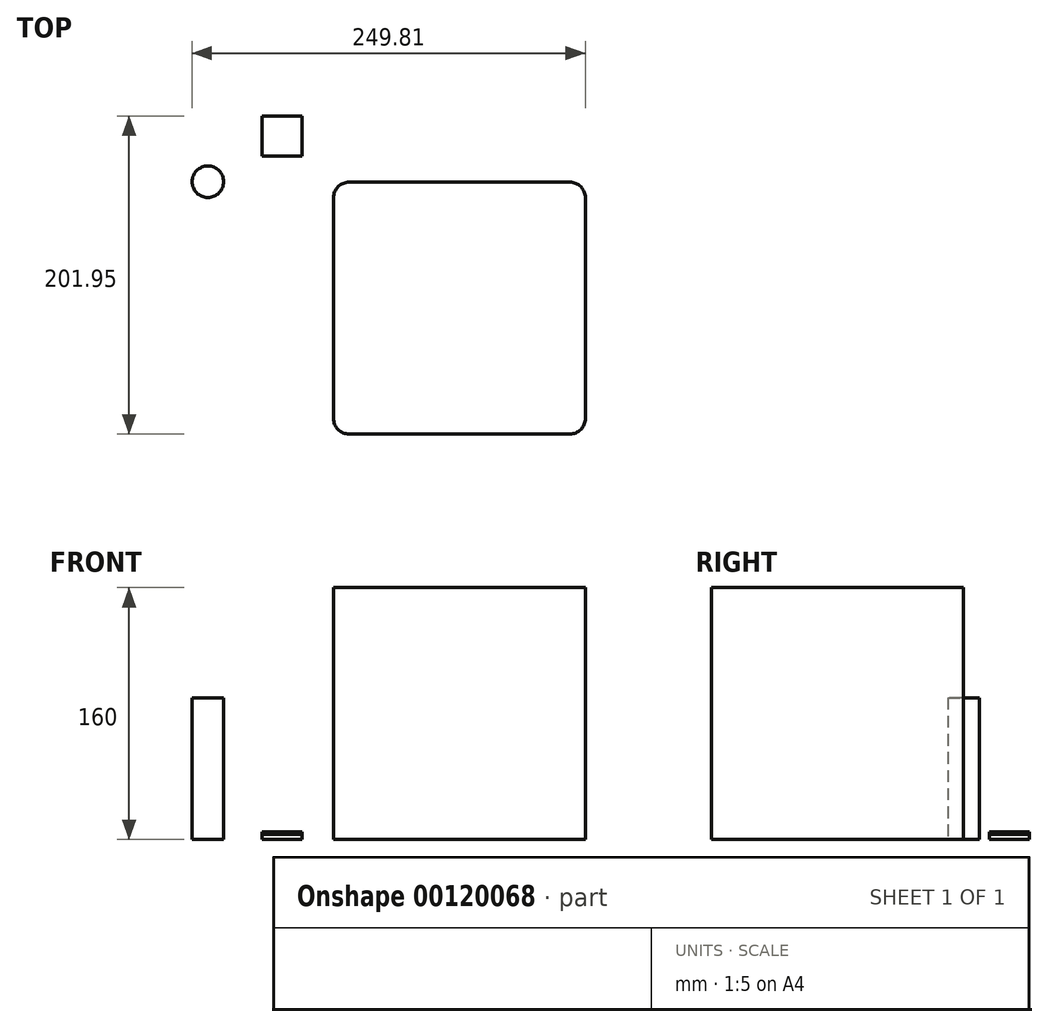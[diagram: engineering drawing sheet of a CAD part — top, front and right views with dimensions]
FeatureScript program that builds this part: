
annotation { "Feature Type Name" : "Feature", "Feature Type Description" : "" }
export const myFeature = defineFeature(function(context is Context, id is Id, definition is map)
    precondition{}
    {
        {
            var Q0;
            Q0=qCreatedBy(makeId("Top.planeOp"),FACE);
            var sketch = newSketch(context, id + "F0", { "sketchPlane" : qUnion([Q0])});
            skLineSegment(sketch, "E0.bottom", {"start": v(12.7, -12.7) * mm, "end": v(-12.7, -12.7) * mm});
            skLineSegment(sketch, "E0.top", {"start": v(12.7, 12.7) * mm, "end": v(-12.7, 12.7) * mm});
            skLineSegment(sketch, "E0.left", {"start": v(12.7, -12.7) * mm, "end": v(12.7, 12.7) * mm});
            skLineSegment(sketch, "E0.right", {"start": v(-12.7, -12.7) * mm, "end": v(-12.7, 12.7) * mm});
            skPoint(sketch, "E0.middle", {"position": v(0, 0) * mm});
            skSolve(sketch);
        }
        {
            var Q0;
            Q0 = qSketchRegion(id + "F0", true);
            extrude(context, id + "F1", {"entities" : qUnion([Q0]), "depth" : 3.17 * mm});
        }
        {
            var Q0;
            Q0=makeQuery(id+"F1.opExtrude","CAP_FACE",FACE,{"disambiguationData":[OSD([sQuery(id+"F0.wireOp",EDGE,"E0.bottom"),sQuery(id+"F0.wireOp",EDGE,"E0.top"),sQuery(id+"F0.wireOp",EDGE,"E0.left"),sQuery(id+"F0.wireOp",EDGE,"E0.right")])],"isStart":false});
            var sketch = newSketch(context, id + "F2", { "sketchPlane" : qUnion([Q0])});
            skLineSegment(sketch, "E1.bottom", {"start": v(-12.7, 12.7) * mm, "end": v(12.7, 12.7) * mm});
            skLineSegment(sketch, "E1.top", {"start": v(-12.7, -12.7) * mm, "end": v(12.7, -12.7) * mm});
            skLineSegment(sketch, "E1.left", {"start": v(-12.7, 12.7) * mm, "end": v(-12.7, -12.7) * mm});
            skLineSegment(sketch, "E1.right", {"start": v(12.7, 12.7) * mm, "end": v(12.7, -12.7) * mm});
            skSolve(sketch);
        }
        {
            var Q0;
            Q0 = qSketchRegion(id + "F2", true);
            extrude(context, id + "F3", {"entities" : qUnion([Q0]), "depth" : 1.59 * mm});
        }
        {
            var Q0;
            Q0=qCreatedBy(makeId("Top.planeOp"),FACE);
            var sketch = newSketch(context, id + "F4", { "sketchPlane" : qUnion([Q0])});
            skCircle(sketch, "E2", {"center": v(-47.05, -28.98) * mm, "radius": 10 * mm});
            skSolve(sketch);
        }
        {
            var Q0;
            Q0 = qSketchRegion(id + "F4", true);
            extrude(context, id + "F5", {"entities" : qUnion([Q0]), "depth" : 1 * mm});
        }
        {
            var Q0;
            Q0=makeQuery(id+"F5.opExtrude","CAP_FACE",FACE,{"disambiguationData":[OSD([sQuery(id+"F4.wireOp",EDGE,"E2")])],"isStart":false});
            var sketch = newSketch(context, id + "F6", { "sketchPlane" : qUnion([Q0])});
            skCircle(sketch, "E3", {"center": v(-47.05, -28.98) * mm, "radius": 9 * mm});
            skSolve(sketch);
        }
        {
            var Q0;
            Q0 = qSketchRegion(id + "F6", true);
            extrude(context, id + "F7", {"entities" : qUnion([Q0]), "operationType" : NewBodyOperationType.ADD, "depth" : 88 * mm});
        }
        {
            var Q0;
            Q0=makeQuery(id+"F5.opExtrude","CAP_FACE",FACE,{"disambiguationData":[OSD([sQuery(id+"F4.wireOp",EDGE,"E2")])],"isStart":false});
            var sketch = newSketch(context, id + "F8", { "sketchPlane" : qUnion([Q0])});
            skCircle(sketch, "E4", {"center": v(-47.05, -28.98) * mm, "radius": 10 * mm});
            skCircle(sketch, "E5", {"center": v(-47.05, -28.98) * mm, "radius": 9 * mm});
            skSolve(sketch);
        }
        {
            var Q0;
            Q0 = qSketchRegion(id + "F8", true);
            var Q1;
            Q1=makeQuery(id+"F7.opExtrude","CAP_FACE",FACE,{"disambiguationData":[OSD([sQuery(id+"F6.wireOp",EDGE,"E3")])],"isStart":false});
            extrude(context, id + "F9", {"entities" : qUnion([Q0]), "endBound" : BoundingType.UP_TO_SURFACE, "endBoundEntityFace" : qUnion([Q1]), "depth" : 48 * mm});
        }
        {
            var Q0;
            Q0=makeQuery(id+"F9.opExtrude","CAP_FACE",FACE,{"disambiguationData":[OSD([sQuery(id+"F8.wireOp",EDGE,"E4"),sQuery(id+"F8.wireOp",EDGE,"E5")])],"isStart":false});
            var sketch = newSketch(context, id + "F10", { "sketchPlane" : qUnion([Q0])});
            skCircle(sketch, "E6", {"center": v(-47.05, -28.98) * mm, "radius": 10 * mm});
            skSolve(sketch);
        }
        {
            var Q0;
            Q0 = qSketchRegion(id + "F10", true);
            extrude(context, id + "F11", {"entities" : qUnion([Q0]), "operationType" : NewBodyOperationType.ADD, "depth" : 1 * mm});
        }
        {
            var Q0;
            Q0=qCreatedBy(makeId("Top.planeOp"),FACE);
            var sketch = newSketch(context, id + "F12", { "sketchPlane" : qUnion([Q0])});
            skLineSegment(sketch, "E7.bottom", {"start": v(32.76, -29.25) * mm, "end": v(192.76, -29.25) * mm});
            skLineSegment(sketch, "E7.top", {"start": v(32.76, -189.25) * mm, "end": v(192.76, -189.25) * mm});
            skLineSegment(sketch, "E7.left", {"start": v(32.76, -29.25) * mm, "end": v(32.76, -189.25) * mm});
            skLineSegment(sketch, "E7.right", {"start": v(192.76, -29.25) * mm, "end": v(192.76, -189.25) * mm});
            skSolve(sketch);
        }
        {
            var Q0;
            Q0 = qSketchRegion(id + "F12", true);
            extrude(context, id + "F13", {"entities" : qUnion([Q0]), "depth" : 160 * mm});
        }
        {
            var Q0;
            Q0=makeQuery(id+"F13.opExtrude","SWEPT_EDGE",EDGE,{"disambiguationData":[OSD([sQuery(id+"F12.wireOp",EDGE,"E7.top"),sQuery(id+"F12.wireOp",EDGE,"E7.left")])]});
            var Q1;
            Q1=makeQuery(id+"F13.opExtrude","SWEPT_EDGE",EDGE,{"disambiguationData":[OSD([sQuery(id+"F12.wireOp",EDGE,"E7.top"),sQuery(id+"F12.wireOp",EDGE,"E7.right")])]});
            var Q2;
            Q2=makeQuery(id+"F13.opExtrude","SWEPT_EDGE",EDGE,{"disambiguationData":[OSD([sQuery(id+"F12.wireOp",EDGE,"E7.bottom"),sQuery(id+"F12.wireOp",EDGE,"E7.right")])]});
            var Q3;
            Q3=makeQuery(id+"F13.opExtrude","SWEPT_EDGE",EDGE,{"disambiguationData":[OSD([sQuery(id+"F12.wireOp",EDGE,"E7.bottom"),sQuery(id+"F12.wireOp",EDGE,"E7.left")])]});
            fillet(context, id + "F14", {"entities" : qUnion([Q0, Q1, Q2, Q3]), "radius" : 10 * mm, "tangentPropagation" : true, "allowEdgeOverflow" : false});
        }
    });
